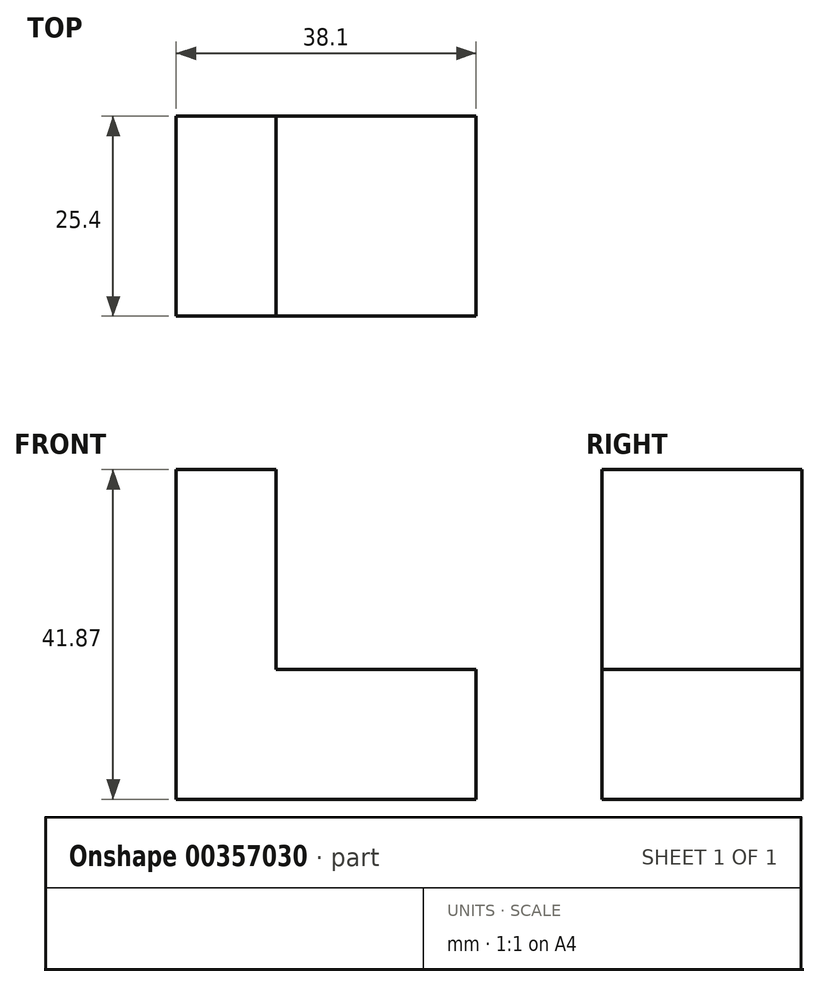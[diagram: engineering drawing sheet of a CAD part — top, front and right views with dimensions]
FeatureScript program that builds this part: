
annotation { "Feature Type Name" : "Feature", "Feature Type Description" : "" }
export const myFeature = defineFeature(function(context is Context, id is Id, definition is map)
    precondition{}
    {
        {
            var Q0;
            Q0=qCreatedBy(makeId("Front.planeOp"),FACE);
            var sketch = newSketch(context, id + "F0", { "sketchPlane" : qUnion([Q0])});
            skLineSegment(sketch, "E0", {"start": v(0, 0) * mm, "end": v(38.1, 0) * mm});
            skLineSegment(sketch, "E1", {"start": v(38.1, 0) * mm, "end": v(38.1, 16.47) * mm});
            skLineSegment(sketch, "E2", {"start": v(38.1, 16.47) * mm, "end": v(12.7, 16.47) * mm});
            skLineSegment(sketch, "E3", {"start": v(12.7, 16.47) * mm, "end": v(12.7, 41.87) * mm});
            skLineSegment(sketch, "E4", {"start": v(12.7, 41.87) * mm, "end": v(0, 41.87) * mm});
            skLineSegment(sketch, "E5", {"start": v(0, 41.87) * mm, "end": v(0, 0) * mm});
            skSolve(sketch);
        }
        {
            var Q0;
            Q0 = qSketchRegion(id + "F0", true);
            extrude(context, id + "F1", {"entities" : qUnion([Q0]), "depth" : 25.4 * mm});
        }
    });
